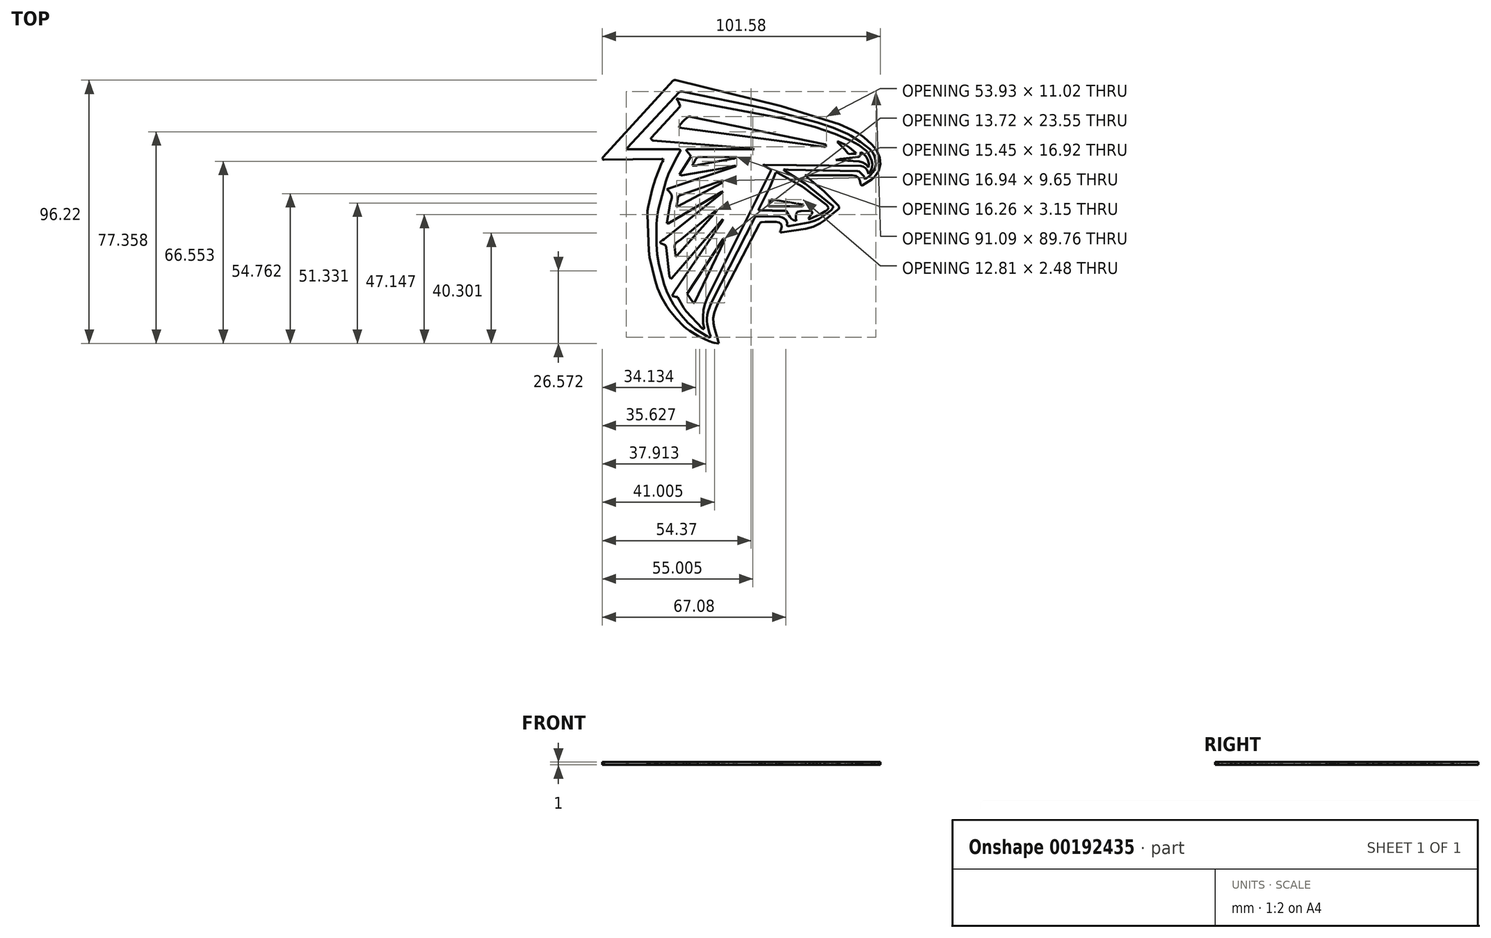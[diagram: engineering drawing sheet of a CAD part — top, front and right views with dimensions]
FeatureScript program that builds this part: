
annotation { "Feature Type Name" : "Feature", "Feature Type Description" : "" }
export const myFeature = defineFeature(function(context is Context, id is Id, definition is map)
    precondition{}
    {
        {
            var Q0;
            Q0=qCreatedBy(makeId("Top.planeOp"),FACE);
            var sketch = newSketch(context, id + "F0", { "sketchPlane" : qUnion([Q0])});
            skLineSegment(sketch, "E0", {"start": v(23.28, 13.3) * mm, "end": v(30.3, 7.5) * mm});
            skLineSegment(sketch, "E1", {"start": v(30.3, 7.5) * mm, "end": v(35.43, 2.3) * mm});
            skLineSegment(sketch, "E2", {"start": v(35.43, 2.3) * mm, "end": v(35.74, 1.85) * mm});
            skLineSegment(sketch, "E3", {"start": v(35.74, 1.85) * mm, "end": v(35.77, 1.44) * mm});
            skLineSegment(sketch, "E4", {"start": v(35.77, 1.44) * mm, "end": v(35.59, 1.07) * mm});
            skLineSegment(sketch, "E5", {"start": v(35.59, 1.07) * mm, "end": v(35.26, 0.74) * mm});
            skLineSegment(sketch, "E6", {"start": v(35.26, 0.74) * mm, "end": v(30.53, -3.08) * mm});
            skLineSegment(sketch, "E7", {"start": v(30.53, -3.08) * mm, "end": v(28.87, -4.22) * mm});
            skLineSegment(sketch, "E8", {"start": v(28.87, -4.22) * mm, "end": v(27.63, -4.88) * mm});
            skLineSegment(sketch, "E9", {"start": v(27.63, -4.88) * mm, "end": v(26.3, -5.42) * mm});
            skLineSegment(sketch, "E10", {"start": v(26.3, -5.42) * mm, "end": v(24.92, -5.85) * mm});
            skLineSegment(sketch, "E11", {"start": v(24.92, -5.85) * mm, "end": v(23.52, -6.18) * mm});
            skLineSegment(sketch, "E12", {"start": v(23.52, -6.18) * mm, "end": v(14.87, -7.46) * mm});
            skLineSegment(sketch, "E13", {"start": v(14.87, -7.46) * mm, "end": v(14.3, -7.46) * mm});
            skLineSegment(sketch, "E14", {"start": v(14.3, -7.46) * mm, "end": v(14.16, -7.29) * mm});
            skLineSegment(sketch, "E15", {"start": v(14.16, -7.29) * mm, "end": v(14.26, -6.99) * mm});
            skLineSegment(sketch, "E16", {"start": v(14.26, -6.99) * mm, "end": v(14.47, -6.6) * mm});
            skLineSegment(sketch, "E17", {"start": v(14.47, -6.6) * mm, "end": v(14.8, -5.5) * mm});
            skLineSegment(sketch, "E18", {"start": v(14.8, -5.5) * mm, "end": v(14.6, -4.6) * mm});
            skLineSegment(sketch, "E19", {"start": v(14.6, -4.6) * mm, "end": v(13.92, -3.95) * mm});
            skLineSegment(sketch, "E20", {"start": v(13.92, -3.95) * mm, "end": v(12.8, -3.69) * mm});
            skLineSegment(sketch, "E21", {"start": v(12.8, -3.69) * mm, "end": v(8.7, -3.66) * mm});
            skLineSegment(sketch, "E22", {"start": v(8.7, -3.66) * mm, "end": v(7.35, -3.78) * mm});
            skLineSegment(sketch, "E23", {"start": v(7.35, -3.78) * mm, "end": v(6.97, -3.98) * mm});
            skLineSegment(sketch, "E24", {"start": v(6.97, -3.98) * mm, "end": v(6.6, -4.42) * mm});
            skLineSegment(sketch, "E25", {"start": v(6.6, -4.42) * mm, "end": v(-8.52, -33.44) * mm});
            skLineSegment(sketch, "E26", {"start": v(-8.52, -33.44) * mm, "end": v(-9.27, -35.2) * mm});
            skLineSegment(sketch, "E27", {"start": v(-9.27, -35.2) * mm, "end": v(-9.87, -37) * mm});
            skLineSegment(sketch, "E28", {"start": v(-9.87, -37) * mm, "end": v(-10.2, -38.85) * mm});
            skLineSegment(sketch, "E29", {"start": v(-10.2, -38.85) * mm, "end": v(-10.15, -40.75) * mm});
            skLineSegment(sketch, "E30", {"start": v(-10.15, -40.75) * mm, "end": v(-9.86, -42.23) * mm});
            skLineSegment(sketch, "E31", {"start": v(-9.86, -42.23) * mm, "end": v(-8.51, -46.97) * mm});
            skLineSegment(sketch, "E32", {"start": v(-8.51, -46.97) * mm, "end": v(-8.26, -48.11) * mm});
            skLineSegment(sketch, "E33", {"start": v(-8.26, -48.11) * mm, "end": v(-9.85, -47.87) * mm});
            skLineSegment(sketch, "E34", {"start": v(-9.85, -47.87) * mm, "end": v(-10.37, -47.73) * mm});
            skLineSegment(sketch, "E35", {"start": v(-10.37, -47.73) * mm, "end": v(-11.81, -47.2) * mm});
            skLineSegment(sketch, "E36", {"start": v(-11.81, -47.2) * mm, "end": v(-15.84, -45.4) * mm});
            skLineSegment(sketch, "E37", {"start": v(-15.84, -45.4) * mm, "end": v(-18.95, -43.47) * mm});
            skLineSegment(sketch, "E38", {"start": v(-18.95, -43.47) * mm, "end": v(-20.04, -42.66) * mm});
            skLineSegment(sketch, "E39", {"start": v(-20.04, -42.66) * mm, "end": v(-21.05, -41.78) * mm});
            skLineSegment(sketch, "E40", {"start": v(-21.05, -41.78) * mm, "end": v(-23.76, -38.96) * mm});
            skLineSegment(sketch, "E41", {"start": v(-23.76, -38.96) * mm, "end": v(-26.2, -35.92) * mm});
            skLineSegment(sketch, "E42", {"start": v(-26.2, -35.92) * mm, "end": v(-27.26, -34.37) * mm});
            skLineSegment(sketch, "E43", {"start": v(-27.26, -34.37) * mm, "end": v(-29.11, -31.1) * mm});
            skLineSegment(sketch, "E44", {"start": v(-29.11, -31.1) * mm, "end": v(-30.55, -28) * mm});
            skLineSegment(sketch, "E45", {"start": v(-30.55, -28) * mm, "end": v(-31.52, -25.04) * mm});
            skLineSegment(sketch, "E46", {"start": v(-31.52, -25.04) * mm, "end": v(-33.47, -16.6) * mm});
            skLineSegment(sketch, "E47", {"start": v(-33.47, -16.6) * mm, "end": v(-33.8, -14.27) * mm});
            skLineSegment(sketch, "E48", {"start": v(-33.8, -14.27) * mm, "end": v(-34.31, -1.16) * mm});
            skLineSegment(sketch, "E49", {"start": v(-34.31, -1.16) * mm, "end": v(-34.24, 0.31) * mm});
            skLineSegment(sketch, "E50", {"start": v(-34.24, 0.31) * mm, "end": v(-34.04, 1.8) * mm});
            skLineSegment(sketch, "E51", {"start": v(-34.04, 1.8) * mm, "end": v(-32.46, 8.38) * mm});
            skLineSegment(sketch, "E52", {"start": v(-32.46, 8.38) * mm, "end": v(-31.33, 12) * mm});
            skLineSegment(sketch, "E53", {"start": v(-31.33, 12) * mm, "end": v(-29.05, 17.9) * mm});
            skLineSegment(sketch, "E54", {"start": v(-29.05, 17.9) * mm, "end": v(-29, 18) * mm});
            skLineSegment(sketch, "E55", {"start": v(-29, 18) * mm, "end": v(-28.93, 18.1) * mm});
            skLineSegment(sketch, "E56", {"start": v(-28.93, 18.1) * mm, "end": v(-28.78, 18.29) * mm});
            skLineSegment(sketch, "E57", {"start": v(-28.78, 18.29) * mm, "end": v(-28.44, 18.96) * mm});
            skLineSegment(sketch, "E58", {"start": v(-28.44, 18.96) * mm, "end": v(-28.57, 19.27) * mm});
            skLineSegment(sketch, "E59", {"start": v(-28.57, 19.27) * mm, "end": v(-29, 19.36) * mm});
            skLineSegment(sketch, "E60", {"start": v(-29, 19.36) * mm, "end": v(-50.12, 19.08) * mm});
            skLineSegment(sketch, "E61", {"start": v(-50.12, 19.08) * mm, "end": v(-50.29, 19.1) * mm});
            skLineSegment(sketch, "E62", {"start": v(-50.29, 19.1) * mm, "end": v(-50.45, 19.14) * mm});
            skLineSegment(sketch, "E63", {"start": v(-50.45, 19.14) * mm, "end": v(-50.8, 19.24) * mm});
            skLineSegment(sketch, "E64", {"start": v(-50.8, 19.24) * mm, "end": v(-50.67, 19.59) * mm});
            skLineSegment(sketch, "E65", {"start": v(-50.67, 19.59) * mm, "end": v(-50.6, 19.75) * mm});
            skLineSegment(sketch, "E66", {"start": v(-50.6, 19.75) * mm, "end": v(-50.5, 19.9) * mm});
            skLineSegment(sketch, "E67", {"start": v(-50.5, 19.9) * mm, "end": v(-24.84, 47.95) * mm});
            skLineSegment(sketch, "E68", {"start": v(-24.84, 47.95) * mm, "end": v(-24.67, 48.06) * mm});
            skLineSegment(sketch, "E69", {"start": v(-24.67, 48.06) * mm, "end": v(-24.44, 48.1) * mm});
            skLineSegment(sketch, "E70", {"start": v(-24.44, 48.1) * mm, "end": v(-24.19, 48.11) * mm});
            skLineSegment(sketch, "E71", {"start": v(-24.19, 48.11) * mm, "end": v(-23.95, 48.1) * mm});
            skLineSegment(sketch, "E72", {"start": v(-23.95, 48.1) * mm, "end": v(14.66, 38.66) * mm});
            skLineSegment(sketch, "E73", {"start": v(14.66, 38.66) * mm, "end": v(35.83, 31.94) * mm});
            skLineSegment(sketch, "E74", {"start": v(35.83, 31.94) * mm, "end": v(40.3, 30) * mm});
            skLineSegment(sketch, "E75", {"start": v(40.3, 30) * mm, "end": v(42.7, 28.71) * mm});
            skLineSegment(sketch, "E76", {"start": v(42.7, 28.71) * mm, "end": v(43.83, 28) * mm});
            skLineSegment(sketch, "E77", {"start": v(43.83, 28) * mm, "end": v(44.9, 27.19) * mm});
            skLineSegment(sketch, "E78", {"start": v(44.9, 27.19) * mm, "end": v(47.52, 24.76) * mm});
            skLineSegment(sketch, "E79", {"start": v(47.52, 24.76) * mm, "end": v(48.7, 23.44) * mm});
            skLineSegment(sketch, "E80", {"start": v(48.7, 23.44) * mm, "end": v(49.68, 22) * mm});
            skLineSegment(sketch, "E81", {"start": v(49.68, 22) * mm, "end": v(50.55, 19.82) * mm});
            skLineSegment(sketch, "E82", {"start": v(50.55, 19.82) * mm, "end": v(50.8, 17.38) * mm});
            skLineSegment(sketch, "E83", {"start": v(50.8, 17.38) * mm, "end": v(50.2, 14.9) * mm});
            skLineSegment(sketch, "E84", {"start": v(50.2, 14.9) * mm, "end": v(48.62, 12.64) * mm});
            skLineSegment(sketch, "E85", {"start": v(48.62, 12.64) * mm, "end": v(47.61, 11.79) * mm});
            skLineSegment(sketch, "E86", {"start": v(47.61, 11.79) * mm, "end": v(44.24, 9.62) * mm});
            skLineSegment(sketch, "E87", {"start": v(44.24, 9.62) * mm, "end": v(44.09, 9.65) * mm});
            skLineSegment(sketch, "E88", {"start": v(44.09, 9.65) * mm, "end": v(43.86, 9.8) * mm});
            skLineSegment(sketch, "E89", {"start": v(43.86, 9.8) * mm, "end": v(43.64, 9.98) * mm});
            skLineSegment(sketch, "E90", {"start": v(43.64, 9.98) * mm, "end": v(43.55, 10.14) * mm});
            skLineSegment(sketch, "E91", {"start": v(43.55, 10.14) * mm, "end": v(43.37, 11.44) * mm});
            skLineSegment(sketch, "E92", {"start": v(43.37, 11.44) * mm, "end": v(42.82, 12.43) * mm});
            skLineSegment(sketch, "E93", {"start": v(42.82, 12.43) * mm, "end": v(41.89, 13.06) * mm});
            skLineSegment(sketch, "E94", {"start": v(41.89, 13.06) * mm, "end": v(40.58, 13.3) * mm});
            skLineSegment(sketch, "E95", {"start": v(40.58, 13.3) * mm, "end": v(23.45, 13.34) * mm});
            skLineSegment(sketch, "E96", {"start": v(23.45, 13.34) * mm, "end": v(23.37, 13.33) * mm});
            skLineSegment(sketch, "E97", {"start": v(23.37, 13.33) * mm, "end": v(23.31, 13.32) * mm});
            skLineSegment(sketch, "E98", {"start": v(23.31, 13.32) * mm, "end": v(23.28, 13.3) * mm});
            skLineSegment(sketch, "E99", {"start": v(23.28, 13.3) * mm, "end": v(23.28, 13.3) * mm});
            skLineSegment(sketch, "E100", {"start": v(-32.1, 22.82) * mm, "end": v(-22.6, 22.8) * mm});
            skLineSegment(sketch, "E101", {"start": v(-22.6, 22.8) * mm, "end": v(-22.47, 22.73) * mm});
            skLineSegment(sketch, "E102", {"start": v(-22.47, 22.73) * mm, "end": v(-22.32, 22.58) * mm});
            skLineSegment(sketch, "E103", {"start": v(-22.32, 22.58) * mm, "end": v(-22.2, 22.42) * mm});
            skLineSegment(sketch, "E104", {"start": v(-22.2, 22.42) * mm, "end": v(-22.18, 22.32) * mm});
            skLineSegment(sketch, "E105", {"start": v(-22.18, 22.32) * mm, "end": v(-23.47, 20.09) * mm});
            skLineSegment(sketch, "E106", {"start": v(-23.47, 20.09) * mm, "end": v(-26.46, 14.04) * mm});
            skLineSegment(sketch, "E107", {"start": v(-26.46, 14.04) * mm, "end": v(-27.54, 11.12) * mm});
            skLineSegment(sketch, "E108", {"start": v(-27.54, 11.12) * mm, "end": v(-30.26, 0.8) * mm});
            skLineSegment(sketch, "E109", {"start": v(-30.26, 0.8) * mm, "end": v(-30.7, -1.77) * mm});
            skLineSegment(sketch, "E110", {"start": v(-30.7, -1.77) * mm, "end": v(-30.9, -4.37) * mm});
            skLineSegment(sketch, "E111", {"start": v(-30.9, -4.37) * mm, "end": v(-30.97, -11.85) * mm});
            skLineSegment(sketch, "E112", {"start": v(-30.97, -11.85) * mm, "end": v(-30.7, -15.58) * mm});
            skLineSegment(sketch, "E113", {"start": v(-30.7, -15.58) * mm, "end": v(-30.04, -19.28) * mm});
            skLineSegment(sketch, "E114", {"start": v(-30.04, -19.28) * mm, "end": v(-28.11, -26.54) * mm});
            skLineSegment(sketch, "E115", {"start": v(-28.11, -26.54) * mm, "end": v(-27.23, -29) * mm});
            skLineSegment(sketch, "E116", {"start": v(-27.23, -29) * mm, "end": v(-26.14, -31.4) * mm});
            skLineSegment(sketch, "E117", {"start": v(-26.14, -31.4) * mm, "end": v(-24.7, -33.94) * mm});
            skLineSegment(sketch, "E118", {"start": v(-24.7, -33.94) * mm, "end": v(-23.9, -35.17) * mm});
            skLineSegment(sketch, "E119", {"start": v(-23.9, -35.17) * mm, "end": v(-21.91, -37.77) * mm});
            skLineSegment(sketch, "E120", {"start": v(-21.91, -37.77) * mm, "end": v(-19.5, -40.48) * mm});
            skLineSegment(sketch, "E121", {"start": v(-19.5, -40.48) * mm, "end": v(-18.18, -41.72) * mm});
            skLineSegment(sketch, "E122", {"start": v(-18.18, -41.72) * mm, "end": v(-16.84, -42.77) * mm});
            skLineSegment(sketch, "E123", {"start": v(-16.84, -42.77) * mm, "end": v(-12.3, -45.64) * mm});
            skLineSegment(sketch, "E124", {"start": v(-12.3, -45.64) * mm, "end": v(-12.1, -45.73) * mm});
            skLineSegment(sketch, "E125", {"start": v(-12.1, -45.73) * mm, "end": v(-11.88, -45.8) * mm});
            skLineSegment(sketch, "E126", {"start": v(-11.88, -45.8) * mm, "end": v(-11.67, -45.85) * mm});
            skLineSegment(sketch, "E127", {"start": v(-11.67, -45.85) * mm, "end": v(-11.52, -45.83) * mm});
            skLineSegment(sketch, "E128", {"start": v(-11.52, -45.83) * mm, "end": v(-11.35, -45.77) * mm});
            skLineSegment(sketch, "E129", {"start": v(-11.35, -45.77) * mm, "end": v(-11.22, -45.7) * mm});
            skLineSegment(sketch, "E130", {"start": v(-11.22, -45.7) * mm, "end": v(-11.17, -45.65) * mm});
            skLineSegment(sketch, "E131", {"start": v(-11.17, -45.65) * mm, "end": v(-11.72, -43.85) * mm});
            skLineSegment(sketch, "E132", {"start": v(-11.72, -43.85) * mm, "end": v(-12.35, -41.06) * mm});
            skLineSegment(sketch, "E133", {"start": v(-12.35, -41.06) * mm, "end": v(-12.51, -39.97) * mm});
            skLineSegment(sketch, "E134", {"start": v(-12.51, -39.97) * mm, "end": v(-12.54, -38.89) * mm});
            skLineSegment(sketch, "E135", {"start": v(-12.54, -38.89) * mm, "end": v(-12.4, -37.75) * mm});
            skLineSegment(sketch, "E136", {"start": v(-12.4, -37.75) * mm, "end": v(-12.14, -36.61) * mm});
            skLineSegment(sketch, "E137", {"start": v(-12.14, -36.61) * mm, "end": v(-11.4, -34.39) * mm});
            skLineSegment(sketch, "E138", {"start": v(-11.4, -34.39) * mm, "end": v(-10.41, -32.1) * mm});
            skLineSegment(sketch, "E139", {"start": v(-10.41, -32.1) * mm, "end": v(4.69, -2.53) * mm});
            skLineSegment(sketch, "E140", {"start": v(4.69, -2.53) * mm, "end": v(5.03, -2.04) * mm});
            skLineSegment(sketch, "E141", {"start": v(5.03, -2.04) * mm, "end": v(5.38, -1.82) * mm});
            skLineSegment(sketch, "E142", {"start": v(5.38, -1.82) * mm, "end": v(9.67, -1.69) * mm});
            skLineSegment(sketch, "E143", {"start": v(9.67, -1.69) * mm, "end": v(13.96, -1.82) * mm});
            skLineSegment(sketch, "E144", {"start": v(13.96, -1.82) * mm, "end": v(14.88, -1.99) * mm});
            skLineSegment(sketch, "E145", {"start": v(14.88, -1.99) * mm, "end": v(15.71, -2.4) * mm});
            skLineSegment(sketch, "E146", {"start": v(15.71, -2.4) * mm, "end": v(16.37, -3.08) * mm});
            skLineSegment(sketch, "E147", {"start": v(16.37, -3.08) * mm, "end": v(16.76, -4.1) * mm});
            skLineSegment(sketch, "E148", {"start": v(16.76, -4.1) * mm, "end": v(16.72, -4.9) * mm});
            skLineSegment(sketch, "E149", {"start": v(16.72, -4.9) * mm, "end": v(16.91, -5.22) * mm});
            skLineSegment(sketch, "E150", {"start": v(16.91, -5.22) * mm, "end": v(17.53, -5.25) * mm});
            skLineSegment(sketch, "E151", {"start": v(17.53, -5.25) * mm, "end": v(24.58, -3.94) * mm});
            skLineSegment(sketch, "E152", {"start": v(24.58, -3.94) * mm, "end": v(26.85, -3.27) * mm});
            skLineSegment(sketch, "E153", {"start": v(26.85, -3.27) * mm, "end": v(28.45, -2.53) * mm});
            skLineSegment(sketch, "E154", {"start": v(28.45, -2.53) * mm, "end": v(29.96, -1.55) * mm});
            skLineSegment(sketch, "E155", {"start": v(29.96, -1.55) * mm, "end": v(32.9, 0.64) * mm});
            skLineSegment(sketch, "E156", {"start": v(32.9, 0.64) * mm, "end": v(33.17, 0.95) * mm});
            skLineSegment(sketch, "E157", {"start": v(33.17, 0.95) * mm, "end": v(33.41, 1.38) * mm});
            skLineSegment(sketch, "E158", {"start": v(33.41, 1.38) * mm, "end": v(33.56, 1.77) * mm});
            skLineSegment(sketch, "E159", {"start": v(33.56, 1.77) * mm, "end": v(33.57, 1.98) * mm});
            skLineSegment(sketch, "E160", {"start": v(33.57, 1.98) * mm, "end": v(23.37, 10.22) * mm});
            skLineSegment(sketch, "E161", {"start": v(23.37, 10.22) * mm, "end": v(15.86, 14.94) * mm});
            skLineSegment(sketch, "E162", {"start": v(15.86, 14.94) * mm, "end": v(15.75, 15.03) * mm});
            skLineSegment(sketch, "E163", {"start": v(15.75, 15.03) * mm, "end": v(15.66, 15.14) * mm});
            skLineSegment(sketch, "E164", {"start": v(15.66, 15.14) * mm, "end": v(15.48, 15.38) * mm});
            skLineSegment(sketch, "E165", {"start": v(15.48, 15.38) * mm, "end": v(15.72, 15.46) * mm});
            skLineSegment(sketch, "E166", {"start": v(15.72, 15.46) * mm, "end": v(15.83, 15.49) * mm});
            skLineSegment(sketch, "E167", {"start": v(15.83, 15.49) * mm, "end": v(15.94, 15.5) * mm});
            skLineSegment(sketch, "E168", {"start": v(15.94, 15.5) * mm, "end": v(17.22, 15.3) * mm});
            skLineSegment(sketch, "E169", {"start": v(17.22, 15.3) * mm, "end": v(42.44, 14.87) * mm});
            skLineSegment(sketch, "E170", {"start": v(42.44, 14.87) * mm, "end": v(43.05, 14.67) * mm});
            skLineSegment(sketch, "E171", {"start": v(43.05, 14.67) * mm, "end": v(43.63, 14.22) * mm});
            skLineSegment(sketch, "E172", {"start": v(43.63, 14.22) * mm, "end": v(44.78, 13.13) * mm});
            skLineSegment(sketch, "E173", {"start": v(44.78, 13.13) * mm, "end": v(44.93, 12.73) * mm});
            skLineSegment(sketch, "E174", {"start": v(44.93, 12.73) * mm, "end": v(45.02, 12.22) * mm});
            skLineSegment(sketch, "E175", {"start": v(45.02, 12.22) * mm, "end": v(45.29, 11.98) * mm});
            skLineSegment(sketch, "E176", {"start": v(45.29, 11.98) * mm, "end": v(46, 12.38) * mm});
            skLineSegment(sketch, "E177", {"start": v(46, 12.38) * mm, "end": v(47.13, 13.38) * mm});
            skLineSegment(sketch, "E178", {"start": v(47.13, 13.38) * mm, "end": v(48.09, 14.47) * mm});
            skLineSegment(sketch, "E179", {"start": v(48.09, 14.47) * mm, "end": v(48.79, 15.71) * mm});
            skLineSegment(sketch, "E180", {"start": v(48.79, 15.71) * mm, "end": v(49.13, 17.16) * mm});
            skLineSegment(sketch, "E181", {"start": v(49.13, 17.16) * mm, "end": v(49.1, 18.8) * mm});
            skLineSegment(sketch, "E182", {"start": v(49.1, 18.8) * mm, "end": v(48.74, 20.35) * mm});
            skLineSegment(sketch, "E183", {"start": v(48.74, 20.35) * mm, "end": v(48.03, 21.74) * mm});
            skLineSegment(sketch, "E184", {"start": v(48.03, 21.74) * mm, "end": v(46.94, 22.93) * mm});
            skLineSegment(sketch, "E185", {"start": v(46.94, 22.93) * mm, "end": v(43.61, 25.5) * mm});
            skLineSegment(sketch, "E186", {"start": v(43.61, 25.5) * mm, "end": v(40.1, 27.82) * mm});
            skLineSegment(sketch, "E187", {"start": v(40.1, 27.82) * mm, "end": v(38.89, 28.49) * mm});
            skLineSegment(sketch, "E188", {"start": v(38.89, 28.49) * mm, "end": v(33.57, 30.67) * mm});
            skLineSegment(sketch, "E189", {"start": v(33.57, 30.67) * mm, "end": v(27.9, 32.6) * mm});
            skLineSegment(sketch, "E190", {"start": v(27.9, 32.6) * mm, "end": v(8.3, 37.88) * mm});
            skLineSegment(sketch, "E191", {"start": v(8.3, 37.88) * mm, "end": v(-21.55, 43.9) * mm});
            skLineSegment(sketch, "E192", {"start": v(-21.55, 43.9) * mm, "end": v(-22, 43.92) * mm});
            skLineSegment(sketch, "E193", {"start": v(-22, 43.92) * mm, "end": v(-22.42, 43.86) * mm});
            skLineSegment(sketch, "E194", {"start": v(-22.42, 43.86) * mm, "end": v(-22.72, 43.7) * mm});
            skLineSegment(sketch, "E195", {"start": v(-22.72, 43.7) * mm, "end": v(-41.65, 23.37) * mm});
            skLineSegment(sketch, "E196", {"start": v(-41.65, 23.37) * mm, "end": v(-41.74, 23.26) * mm});
            skLineSegment(sketch, "E197", {"start": v(-41.74, 23.26) * mm, "end": v(-41.97, 22.92) * mm});
            skLineSegment(sketch, "E198", {"start": v(-41.97, 22.92) * mm, "end": v(-41.5, 22.83) * mm});
            skLineSegment(sketch, "E199", {"start": v(-41.5, 22.83) * mm, "end": v(-41.35, 22.82) * mm});
            skLineSegment(sketch, "E200", {"start": v(-41.35, 22.82) * mm, "end": v(-32.1, 22.82) * mm});
            skLineSegment(sketch, "E201", {"start": v(-2, 16.83) * mm, "end": v(-4.63, 16.43) * mm});
            skLineSegment(sketch, "E202", {"start": v(-4.63, 16.43) * mm, "end": v(-6.82, 15.92) * mm});
            skLineSegment(sketch, "E203", {"start": v(-6.82, 15.92) * mm, "end": v(-21.55, 13.34) * mm});
            skLineSegment(sketch, "E204", {"start": v(-21.55, 13.34) * mm, "end": v(-21.8, 13.35) * mm});
            skLineSegment(sketch, "E205", {"start": v(-21.8, 13.35) * mm, "end": v(-22.08, 13.41) * mm});
            skLineSegment(sketch, "E206", {"start": v(-22.08, 13.41) * mm, "end": v(-22.62, 13.6) * mm});
            skLineSegment(sketch, "E207", {"start": v(-22.62, 13.6) * mm, "end": v(-18.44, 20.18) * mm});
            skLineSegment(sketch, "E208", {"start": v(-18.44, 20.18) * mm, "end": v(-18.46, 20.38) * mm});
            skLineSegment(sketch, "E209", {"start": v(-18.46, 20.38) * mm, "end": v(-18.61, 20.66) * mm});
            skLineSegment(sketch, "E210", {"start": v(-18.61, 20.66) * mm, "end": v(-19.26, 21.51) * mm});
            skLineSegment(sketch, "E211", {"start": v(-19.26, 21.51) * mm, "end": v(-19.92, 22.25) * mm});
            skLineSegment(sketch, "E212", {"start": v(-19.92, 22.25) * mm, "end": v(-19.98, 22.36) * mm});
            skLineSegment(sketch, "E213", {"start": v(-19.98, 22.36) * mm, "end": v(-20.02, 22.5) * mm});
            skLineSegment(sketch, "E214", {"start": v(-20.02, 22.5) * mm, "end": v(-20.03, 22.61) * mm});
            skLineSegment(sketch, "E215", {"start": v(-20.03, 22.61) * mm, "end": v(-20.02, 22.67) * mm});
            skLineSegment(sketch, "E216", {"start": v(-20.02, 22.67) * mm, "end": v(-19.9, 22.73) * mm});
            skLineSegment(sketch, "E217", {"start": v(-19.9, 22.73) * mm, "end": v(-19.77, 22.78) * mm});
            skLineSegment(sketch, "E218", {"start": v(-19.77, 22.78) * mm, "end": v(-19.64, 22.8) * mm});
            skLineSegment(sketch, "E219", {"start": v(-19.64, 22.8) * mm, "end": v(-19.5, 22.81) * mm});
            skLineSegment(sketch, "E220", {"start": v(-19.5, 22.81) * mm, "end": v(3.8, 22.86) * mm});
            skLineSegment(sketch, "E221", {"start": v(3.8, 22.86) * mm, "end": v(4.69, 22.91) * mm});
            skLineSegment(sketch, "E222", {"start": v(4.69, 22.91) * mm, "end": v(4.15, 23.08) * mm});
            skLineSegment(sketch, "E223", {"start": v(4.15, 23.08) * mm, "end": v(4.08, 23.09) * mm});
            skLineSegment(sketch, "E224", {"start": v(4.08, 23.09) * mm, "end": v(-32.26, 26.04) * mm});
            skLineSegment(sketch, "E225", {"start": v(-32.26, 26.04) * mm, "end": v(-32.5, 26.14) * mm});
            skLineSegment(sketch, "E226", {"start": v(-32.5, 26.14) * mm, "end": v(-32.76, 26.36) * mm});
            skLineSegment(sketch, "E227", {"start": v(-32.76, 26.36) * mm, "end": v(-32.94, 26.6) * mm});
            skLineSegment(sketch, "E228", {"start": v(-32.94, 26.6) * mm, "end": v(-33, 26.78) * mm});
            skLineSegment(sketch, "E229", {"start": v(-33, 26.78) * mm, "end": v(-32.85, 27.06) * mm});
            skLineSegment(sketch, "E230", {"start": v(-32.85, 27.06) * mm, "end": v(-22.39, 38.38) * mm});
            skLineSegment(sketch, "E231", {"start": v(-22.39, 38.38) * mm, "end": v(-22.35, 38.64) * mm});
            skLineSegment(sketch, "E232", {"start": v(-22.35, 38.64) * mm, "end": v(-22.46, 39.02) * mm});
            skLineSegment(sketch, "E233", {"start": v(-22.46, 39.02) * mm, "end": v(-23, 40.2) * mm});
            skLineSegment(sketch, "E234", {"start": v(-23, 40.2) * mm, "end": v(-23.69, 41.35) * mm});
            skLineSegment(sketch, "E235", {"start": v(-23.69, 41.35) * mm, "end": v(14.91, 34.12) * mm});
            skLineSegment(sketch, "E236", {"start": v(14.91, 34.12) * mm, "end": v(26.99, 30.97) * mm});
            skLineSegment(sketch, "E237", {"start": v(26.99, 30.97) * mm, "end": v(34.3, 28.46) * mm});
            skLineSegment(sketch, "E238", {"start": v(34.3, 28.46) * mm, "end": v(40.23, 25.93) * mm});
            skLineSegment(sketch, "E239", {"start": v(40.23, 25.93) * mm, "end": v(43.01, 24.34) * mm});
            skLineSegment(sketch, "E240", {"start": v(43.01, 24.34) * mm, "end": v(45.58, 22.38) * mm});
            skLineSegment(sketch, "E241", {"start": v(45.58, 22.38) * mm, "end": v(46.24, 21.61) * mm});
            skLineSegment(sketch, "E242", {"start": v(46.24, 21.61) * mm, "end": v(46.76, 20.69) * mm});
            skLineSegment(sketch, "E243", {"start": v(46.76, 20.69) * mm, "end": v(47.62, 18.68) * mm});
            skLineSegment(sketch, "E244", {"start": v(47.62, 18.68) * mm, "end": v(47.94, 17.45) * mm});
            skLineSegment(sketch, "E245", {"start": v(47.94, 17.45) * mm, "end": v(47.85, 16.28) * mm});
            skLineSegment(sketch, "E246", {"start": v(47.85, 16.28) * mm, "end": v(47.41, 15.17) * mm});
            skLineSegment(sketch, "E247", {"start": v(47.41, 15.17) * mm, "end": v(46.72, 14.12) * mm});
            skLineSegment(sketch, "E248", {"start": v(46.72, 14.12) * mm, "end": v(46.66, 14.05) * mm});
            skLineSegment(sketch, "E249", {"start": v(46.66, 14.05) * mm, "end": v(46.47, 13.87) * mm});
            skLineSegment(sketch, "E250", {"start": v(46.47, 13.87) * mm, "end": v(46.36, 14.16) * mm});
            skLineSegment(sketch, "E251", {"start": v(46.36, 14.16) * mm, "end": v(46.33, 14.25) * mm});
            skLineSegment(sketch, "E252", {"start": v(46.33, 14.25) * mm, "end": v(45.98, 15.23) * mm});
            skLineSegment(sketch, "E253", {"start": v(45.98, 15.23) * mm, "end": v(45.42, 16.02) * mm});
            skLineSegment(sketch, "E254", {"start": v(45.42, 16.02) * mm, "end": v(44.66, 16.56) * mm});
            skLineSegment(sketch, "E255", {"start": v(44.66, 16.56) * mm, "end": v(43.72, 16.79) * mm});
            skLineSegment(sketch, "E256", {"start": v(43.72, 16.79) * mm, "end": v(8.5, 17.14) * mm});
            skLineSegment(sketch, "E257", {"start": v(8.5, 17.14) * mm, "end": v(8.34, 17.13) * mm});
            skLineSegment(sketch, "E258", {"start": v(8.34, 17.13) * mm, "end": v(7.87, 17.05) * mm});
            skLineSegment(sketch, "E259", {"start": v(7.87, 17.05) * mm, "end": v(10.82, 15.52) * mm});
            skLineSegment(sketch, "E260", {"start": v(10.82, 15.52) * mm, "end": v(10.86, 15.37) * mm});
            skLineSegment(sketch, "E261", {"start": v(10.86, 15.37) * mm, "end": v(10.83, 15.08) * mm});
            skLineSegment(sketch, "E262", {"start": v(10.83, 15.08) * mm, "end": v(10.75, 14.74) * mm});
            skLineSegment(sketch, "E263", {"start": v(10.75, 14.74) * mm, "end": v(10.64, 14.45) * mm});
            skLineSegment(sketch, "E264", {"start": v(10.64, 14.45) * mm, "end": v(-12.4, -31.56) * mm});
            skLineSegment(sketch, "E265", {"start": v(-12.4, -31.56) * mm, "end": v(-13.3, -33.76) * mm});
            skLineSegment(sketch, "E266", {"start": v(-13.3, -33.76) * mm, "end": v(-13.82, -36) * mm});
            skLineSegment(sketch, "E267", {"start": v(-13.82, -36) * mm, "end": v(-13.99, -38.3) * mm});
            skLineSegment(sketch, "E268", {"start": v(-13.99, -38.3) * mm, "end": v(-13.88, -40.66) * mm});
            skLineSegment(sketch, "E269", {"start": v(-13.88, -40.66) * mm, "end": v(-13.6, -42.4) * mm});
            skLineSegment(sketch, "E270", {"start": v(-13.6, -42.4) * mm, "end": v(-13.6, -42.5) * mm});
            skLineSegment(sketch, "E271", {"start": v(-13.6, -42.5) * mm, "end": v(-13.6, -42.62) * mm});
            skLineSegment(sketch, "E272", {"start": v(-13.6, -42.62) * mm, "end": v(-13.64, -42.71) * mm});
            skLineSegment(sketch, "E273", {"start": v(-13.64, -42.71) * mm, "end": v(-13.68, -42.76) * mm});
            skLineSegment(sketch, "E274", {"start": v(-13.68, -42.76) * mm, "end": v(-13.8, -42.79) * mm});
            skLineSegment(sketch, "E275", {"start": v(-13.8, -42.79) * mm, "end": v(-13.92, -42.79) * mm});
            skLineSegment(sketch, "E276", {"start": v(-13.92, -42.79) * mm, "end": v(-14.04, -42.77) * mm});
            skLineSegment(sketch, "E277", {"start": v(-14.04, -42.77) * mm, "end": v(-14.13, -42.72) * mm});
            skLineSegment(sketch, "E278", {"start": v(-14.13, -42.72) * mm, "end": v(-20.2, -36.3) * mm});
            skLineSegment(sketch, "E279", {"start": v(-20.2, -36.3) * mm, "end": v(-21.03, -35.12) * mm});
            skLineSegment(sketch, "E280", {"start": v(-21.03, -35.12) * mm, "end": v(-23.15, -31.26) * mm});
            skLineSegment(sketch, "E281", {"start": v(-23.15, -31.26) * mm, "end": v(-23.26, -31.18) * mm});
            skLineSegment(sketch, "E282", {"start": v(-23.26, -31.18) * mm, "end": v(-23.44, -31.14) * mm});
            skLineSegment(sketch, "E283", {"start": v(-23.44, -31.14) * mm, "end": v(-23.83, -31.08) * mm});
            skLineSegment(sketch, "E284", {"start": v(-23.83, -31.08) * mm, "end": v(-25.27, -30.7) * mm});
            skLineSegment(sketch, "E285", {"start": v(-25.27, -30.7) * mm, "end": v(-24.56, -29.51) * mm});
            skLineSegment(sketch, "E286", {"start": v(-24.56, -29.51) * mm, "end": v(-6.73, -3.24) * mm});
            skLineSegment(sketch, "E287", {"start": v(-6.73, -3.24) * mm, "end": v(-6.7, -3.15) * mm});
            skLineSegment(sketch, "E288", {"start": v(-6.7, -3.15) * mm, "end": v(-6.7, -3.03) * mm});
            skLineSegment(sketch, "E289", {"start": v(-6.7, -3.03) * mm, "end": v(-6.72, -2.8) * mm});
            skLineSegment(sketch, "E290", {"start": v(-6.72, -2.8) * mm, "end": v(-6.93, -2.98) * mm});
            skLineSegment(sketch, "E291", {"start": v(-6.93, -2.98) * mm, "end": v(-25.36, -24.28) * mm});
            skLineSegment(sketch, "E292", {"start": v(-25.36, -24.28) * mm, "end": v(-25.45, -24.35) * mm});
            skLineSegment(sketch, "E293", {"start": v(-25.45, -24.35) * mm, "end": v(-25.58, -24.42) * mm});
            skLineSegment(sketch, "E294", {"start": v(-25.58, -24.42) * mm, "end": v(-25.7, -24.46) * mm});
            skLineSegment(sketch, "E295", {"start": v(-25.7, -24.46) * mm, "end": v(-25.75, -24.47) * mm});
            skLineSegment(sketch, "E296", {"start": v(-25.75, -24.47) * mm, "end": v(-26.03, -24) * mm});
            skLineSegment(sketch, "E297", {"start": v(-26.03, -24) * mm, "end": v(-26.14, -23.76) * mm});
            skLineSegment(sketch, "E298", {"start": v(-26.14, -23.76) * mm, "end": v(-26.2, -23.52) * mm});
            skLineSegment(sketch, "E299", {"start": v(-26.2, -23.52) * mm, "end": v(-27.4, -13.07) * mm});
            skLineSegment(sketch, "E300", {"start": v(-27.4, -13.07) * mm, "end": v(-27.51, -12.55) * mm});
            skLineSegment(sketch, "E301", {"start": v(-27.51, -12.55) * mm, "end": v(-27.62, -12.37) * mm});
            skLineSegment(sketch, "E302", {"start": v(-27.62, -12.37) * mm, "end": v(-27.8, -12.2) * mm});
            skLineSegment(sketch, "E303", {"start": v(-27.8, -12.2) * mm, "end": v(-28.04, -12.08) * mm});
            skLineSegment(sketch, "E304", {"start": v(-28.04, -12.08) * mm, "end": v(-28.27, -12) * mm});
            skLineSegment(sketch, "E305", {"start": v(-28.27, -12) * mm, "end": v(-29.51, -11.45) * mm});
            skLineSegment(sketch, "E306", {"start": v(-29.51, -11.45) * mm, "end": v(-29.5, -10.93) * mm});
            skLineSegment(sketch, "E307", {"start": v(-29.5, -10.93) * mm, "end": v(-28.85, -10.45) * mm});
            skLineSegment(sketch, "E308", {"start": v(-28.85, -10.45) * mm, "end": v(-28.22, -10.05) * mm});
            skLineSegment(sketch, "E309", {"start": v(-28.22, -10.05) * mm, "end": v(-6.9, 7.04) * mm});
            skLineSegment(sketch, "E310", {"start": v(-6.9, 7.04) * mm, "end": v(-6.85, 7.1) * mm});
            skLineSegment(sketch, "E311", {"start": v(-6.85, 7.1) * mm, "end": v(-6.7, 7.32) * mm});
            skLineSegment(sketch, "E312", {"start": v(-6.7, 7.32) * mm, "end": v(-6.97, 7.33) * mm});
            skLineSegment(sketch, "E313", {"start": v(-6.97, 7.33) * mm, "end": v(-7.1, 7.33) * mm});
            skLineSegment(sketch, "E314", {"start": v(-7.1, 7.33) * mm, "end": v(-7.22, 7.3) * mm});
            skLineSegment(sketch, "E315", {"start": v(-7.22, 7.3) * mm, "end": v(-26.72, -4.34) * mm});
            skLineSegment(sketch, "E316", {"start": v(-26.72, -4.34) * mm, "end": v(-26.82, -4.32) * mm});
            skLineSegment(sketch, "E317", {"start": v(-26.82, -4.32) * mm, "end": v(-26.97, -4.25) * mm});
            skLineSegment(sketch, "E318", {"start": v(-26.97, -4.25) * mm, "end": v(-27.1, -4.15) * mm});
            skLineSegment(sketch, "E319", {"start": v(-27.1, -4.15) * mm, "end": v(-27.15, -4.08) * mm});
            skLineSegment(sketch, "E320", {"start": v(-27.15, -4.08) * mm, "end": v(-25.98, 2.86) * mm});
            skLineSegment(sketch, "E321", {"start": v(-25.98, 2.86) * mm, "end": v(-25.42, 5.03) * mm});
            skLineSegment(sketch, "E322", {"start": v(-25.42, 5.03) * mm, "end": v(-25.37, 5.74) * mm});
            skLineSegment(sketch, "E323", {"start": v(-25.37, 5.74) * mm, "end": v(-25.5, 6.22) * mm});
            skLineSegment(sketch, "E324", {"start": v(-25.5, 6.22) * mm, "end": v(-25.78, 6.7) * mm});
            skLineSegment(sketch, "E325", {"start": v(-25.78, 6.7) * mm, "end": v(-26.5, 7.62) * mm});
            skLineSegment(sketch, "E326", {"start": v(-26.5, 7.62) * mm, "end": v(-26.64, 7.78) * mm});
            skLineSegment(sketch, "E327", {"start": v(-26.64, 7.78) * mm, "end": v(-26.8, 7.91) * mm});
            skLineSegment(sketch, "E328", {"start": v(-26.8, 7.91) * mm, "end": v(-27.18, 8.17) * mm});
            skLineSegment(sketch, "E329", {"start": v(-27.18, 8.17) * mm, "end": v(-26.71, 8.48) * mm});
            skLineSegment(sketch, "E330", {"start": v(-26.71, 8.48) * mm, "end": v(-26.55, 8.55) * mm});
            skLineSegment(sketch, "E331", {"start": v(-26.55, 8.55) * mm, "end": v(-1.97, 16.64) * mm});
            skLineSegment(sketch, "E332", {"start": v(-1.97, 16.64) * mm, "end": v(-2, 16.83) * mm});
            skLineSegment(sketch, "E333", {"start": v(30.2, 23.76) * mm, "end": v(30.2, 23.75) * mm});
            skLineSegment(sketch, "E334", {"start": v(30.2, 23.75) * mm, "end": v(30.28, 23.74) * mm});
            skLineSegment(sketch, "E335", {"start": v(30.28, 23.74) * mm, "end": v(30.43, 23.74) * mm});
            skLineSegment(sketch, "E336", {"start": v(30.43, 23.74) * mm, "end": v(30.61, 23.76) * mm});
            skLineSegment(sketch, "E337", {"start": v(30.61, 23.76) * mm, "end": v(30.76, 23.8) * mm});
            skLineSegment(sketch, "E338", {"start": v(30.76, 23.8) * mm, "end": v(30.9, 23.89) * mm});
            skLineSegment(sketch, "E339", {"start": v(30.9, 23.89) * mm, "end": v(31.18, 24.07) * mm});
            skLineSegment(sketch, "E340", {"start": v(31.18, 24.07) * mm, "end": v(30.95, 24.4) * mm});
            skLineSegment(sketch, "E341", {"start": v(30.95, 24.4) * mm, "end": v(30.84, 24.55) * mm});
            skLineSegment(sketch, "E342", {"start": v(30.84, 24.55) * mm, "end": v(30.7, 24.63) * mm});
            skLineSegment(sketch, "E343", {"start": v(30.7, 24.63) * mm, "end": v(-18.35, 34.72) * mm});
            skLineSegment(sketch, "E344", {"start": v(-18.35, 34.72) * mm, "end": v(-18.69, 34.76) * mm});
            skLineSegment(sketch, "E345", {"start": v(-18.69, 34.76) * mm, "end": v(-19.04, 34.75) * mm});
            skLineSegment(sketch, "E346", {"start": v(-19.04, 34.75) * mm, "end": v(-19.37, 34.7) * mm});
            skLineSegment(sketch, "E347", {"start": v(-19.37, 34.7) * mm, "end": v(-19.62, 34.56) * mm});
            skLineSegment(sketch, "E348", {"start": v(-19.62, 34.56) * mm, "end": v(-21, 33.23) * mm});
            skLineSegment(sketch, "E349", {"start": v(-21, 33.23) * mm, "end": v(-22.3, 31.83) * mm});
            skLineSegment(sketch, "E350", {"start": v(-22.3, 31.83) * mm, "end": v(-22.46, 31.6) * mm});
            skLineSegment(sketch, "E351", {"start": v(-22.46, 31.6) * mm, "end": v(-22.57, 31.32) * mm});
            skLineSegment(sketch, "E352", {"start": v(-22.57, 31.32) * mm, "end": v(-22.75, 30.73) * mm});
            skLineSegment(sketch, "E353", {"start": v(-22.75, 30.73) * mm, "end": v(30.2, 23.76) * mm});
            skLineSegment(sketch, "E354", {"start": v(-19.74, -29.96) * mm, "end": v(-17.5, -33.28) * mm});
            skLineSegment(sketch, "E355", {"start": v(-17.5, -33.28) * mm, "end": v(-17.41, -33.31) * mm});
            skLineSegment(sketch, "E356", {"start": v(-17.41, -33.31) * mm, "end": v(-17.27, -33.31) * mm});
            skLineSegment(sketch, "E357", {"start": v(-17.27, -33.31) * mm, "end": v(-17.13, -33.29) * mm});
            skLineSegment(sketch, "E358", {"start": v(-17.13, -33.29) * mm, "end": v(-17.05, -33.24) * mm});
            skLineSegment(sketch, "E359", {"start": v(-17.05, -33.24) * mm, "end": v(-6.02, -10.3) * mm});
            skLineSegment(sketch, "E360", {"start": v(-6.02, -10.3) * mm, "end": v(-6.02, -10.18) * mm});
            skLineSegment(sketch, "E361", {"start": v(-6.02, -10.18) * mm, "end": v(-6.08, -10.04) * mm});
            skLineSegment(sketch, "E362", {"start": v(-6.08, -10.04) * mm, "end": v(-6.27, -9.76) * mm});
            skLineSegment(sketch, "E363", {"start": v(-6.27, -9.76) * mm, "end": v(-6.32, -9.77) * mm});
            skLineSegment(sketch, "E364", {"start": v(-6.32, -9.77) * mm, "end": v(-6.43, -9.8) * mm});
            skLineSegment(sketch, "E365", {"start": v(-6.43, -9.8) * mm, "end": v(-6.55, -9.86) * mm});
            skLineSegment(sketch, "E366", {"start": v(-6.55, -9.86) * mm, "end": v(-6.63, -9.93) * mm});
            skLineSegment(sketch, "E367", {"start": v(-6.63, -9.93) * mm, "end": v(-19.74, -29.96) * mm});
            skLineSegment(sketch, "E368", {"start": v(-24.38, -12.74) * mm, "end": v(-24, -16.04) * mm});
            skLineSegment(sketch, "E369", {"start": v(-24, -16.04) * mm, "end": v(-24, -16.1) * mm});
            skLineSegment(sketch, "E370", {"start": v(-24, -16.1) * mm, "end": v(-23.96, -16.16) * mm});
            skLineSegment(sketch, "E371", {"start": v(-23.96, -16.16) * mm, "end": v(-23.9, -16.27) * mm});
            skLineSegment(sketch, "E372", {"start": v(-23.9, -16.27) * mm, "end": v(-23.75, -16.2) * mm});
            skLineSegment(sketch, "E373", {"start": v(-23.75, -16.2) * mm, "end": v(-23.69, -16.18) * mm});
            skLineSegment(sketch, "E374", {"start": v(-23.69, -16.18) * mm, "end": v(-23.63, -16.13) * mm});
            skLineSegment(sketch, "E375", {"start": v(-23.63, -16.13) * mm, "end": v(-9.02, 0.22) * mm});
            skLineSegment(sketch, "E376", {"start": v(-9.02, 0.22) * mm, "end": v(-8.98, 0.31) * mm});
            skLineSegment(sketch, "E377", {"start": v(-8.98, 0.31) * mm, "end": v(-8.96, 0.42) * mm});
            skLineSegment(sketch, "E378", {"start": v(-8.96, 0.42) * mm, "end": v(-8.93, 0.65) * mm});
            skLineSegment(sketch, "E379", {"start": v(-8.93, 0.65) * mm, "end": v(-9.04, 0.65) * mm});
            skLineSegment(sketch, "E380", {"start": v(-9.04, 0.65) * mm, "end": v(-9.09, 0.64) * mm});
            skLineSegment(sketch, "E381", {"start": v(-9.09, 0.64) * mm, "end": v(-9.13, 0.63) * mm});
            skLineSegment(sketch, "E382", {"start": v(-9.13, 0.63) * mm, "end": v(-21.96, -10) * mm});
            skLineSegment(sketch, "E383", {"start": v(-21.96, -10) * mm, "end": v(-23.62, -11.12) * mm});
            skLineSegment(sketch, "E384", {"start": v(-23.62, -11.12) * mm, "end": v(-24.24, -11.8) * mm});
            skLineSegment(sketch, "E385", {"start": v(-24.24, -11.8) * mm, "end": v(-24.38, -12.74) * mm});
            skLineSegment(sketch, "E386", {"start": v(-6.92, 11.48) * mm, "end": v(-22.15, 6.07) * mm});
            skLineSegment(sketch, "E387", {"start": v(-22.15, 6.07) * mm, "end": v(-22.42, 5.95) * mm});
            skLineSegment(sketch, "E388", {"start": v(-22.42, 5.95) * mm, "end": v(-22.68, 5.8) * mm});
            skLineSegment(sketch, "E389", {"start": v(-22.68, 5.8) * mm, "end": v(-22.9, 5.62) * mm});
            skLineSegment(sketch, "E390", {"start": v(-22.9, 5.62) * mm, "end": v(-23.02, 5.41) * mm});
            skLineSegment(sketch, "E391", {"start": v(-23.02, 5.41) * mm, "end": v(-23.63, 2.15) * mm});
            skLineSegment(sketch, "E392", {"start": v(-23.63, 2.15) * mm, "end": v(-23.63, 2.07) * mm});
            skLineSegment(sketch, "E393", {"start": v(-23.63, 2.07) * mm, "end": v(-23.63, 2) * mm});
            skLineSegment(sketch, "E394", {"start": v(-23.63, 2) * mm, "end": v(-23.6, 1.91) * mm});
            skLineSegment(sketch, "E395", {"start": v(-23.6, 1.91) * mm, "end": v(-23.58, 1.84) * mm});
            skLineSegment(sketch, "E396", {"start": v(-23.58, 1.84) * mm, "end": v(-23.56, 1.83) * mm});
            skLineSegment(sketch, "E397", {"start": v(-23.56, 1.83) * mm, "end": v(-23.5, 1.83) * mm});
            skLineSegment(sketch, "E398", {"start": v(-23.5, 1.83) * mm, "end": v(-23.44, 1.83) * mm});
            skLineSegment(sketch, "E399", {"start": v(-23.44, 1.83) * mm, "end": v(-23.38, 1.85) * mm});
            skLineSegment(sketch, "E400", {"start": v(-23.38, 1.85) * mm, "end": v(-7.1, 10.58) * mm});
            skLineSegment(sketch, "E401", {"start": v(-7.1, 10.58) * mm, "end": v(-6.96, 10.7) * mm});
            skLineSegment(sketch, "E402", {"start": v(-6.96, 10.7) * mm, "end": v(-6.86, 10.9) * mm});
            skLineSegment(sketch, "E403", {"start": v(-6.86, 10.9) * mm, "end": v(-6.7, 11.31) * mm});
            skLineSegment(sketch, "E404", {"start": v(-6.7, 11.31) * mm, "end": v(-6.71, 11.34) * mm});
            skLineSegment(sketch, "E405", {"start": v(-6.71, 11.34) * mm, "end": v(-6.92, 11.48) * mm});
            skLineSegment(sketch, "E406", {"start": v(-14.95, 20.02) * mm, "end": v(-15.97, 19.9) * mm});
            skLineSegment(sketch, "E407", {"start": v(-15.97, 19.9) * mm, "end": v(-16.59, 19.34) * mm});
            skLineSegment(sketch, "E408", {"start": v(-16.59, 19.34) * mm, "end": v(-17.4, 17.83) * mm});
            skLineSegment(sketch, "E409", {"start": v(-17.4, 17.83) * mm, "end": v(-17.54, 17.6) * mm});
            skLineSegment(sketch, "E410", {"start": v(-17.54, 17.6) * mm, "end": v(-17.92, 16.88) * mm});
            skLineSegment(sketch, "E411", {"start": v(-17.92, 16.88) * mm, "end": v(-16.93, 16.87) * mm});
            skLineSegment(sketch, "E412", {"start": v(-16.93, 16.87) * mm, "end": v(-16.6, 16.89) * mm});
            skLineSegment(sketch, "E413", {"start": v(-16.6, 16.89) * mm, "end": v(-16.3, 16.94) * mm});
            skLineSegment(sketch, "E414", {"start": v(-16.3, 16.94) * mm, "end": v(-15.7, 17.08) * mm});
            skLineSegment(sketch, "E415", {"start": v(-15.7, 17.08) * mm, "end": v(-3.05, 19.37) * mm});
            skLineSegment(sketch, "E416", {"start": v(-3.05, 19.37) * mm, "end": v(-2.69, 19.48) * mm});
            skLineSegment(sketch, "E417", {"start": v(-2.69, 19.48) * mm, "end": v(-1.65, 20) * mm});
            skLineSegment(sketch, "E418", {"start": v(-1.65, 20) * mm, "end": v(-14.95, 20.02) * mm});
            skLineSegment(sketch, "E419", {"start": v(46.54, 16.29) * mm, "end": v(46.64, 17.52) * mm});
            skLineSegment(sketch, "E420", {"start": v(46.64, 17.52) * mm, "end": v(46.3, 18.9) * mm});
            skLineSegment(sketch, "E421", {"start": v(46.3, 18.9) * mm, "end": v(45.6, 20.23) * mm});
            skLineSegment(sketch, "E422", {"start": v(45.6, 20.23) * mm, "end": v(44.62, 21.24) * mm});
            skLineSegment(sketch, "E423", {"start": v(44.62, 21.24) * mm, "end": v(43.69, 21.83) * mm});
            skLineSegment(sketch, "E424", {"start": v(43.69, 21.83) * mm, "end": v(43.64, 21.24) * mm});
            skLineSegment(sketch, "E425", {"start": v(43.64, 21.24) * mm, "end": v(43.6, 20.95) * mm});
            skLineSegment(sketch, "E426", {"start": v(43.6, 20.95) * mm, "end": v(43.53, 20.67) * mm});
            skLineSegment(sketch, "E427", {"start": v(43.53, 20.67) * mm, "end": v(43.42, 20.47) * mm});
            skLineSegment(sketch, "E428", {"start": v(43.42, 20.47) * mm, "end": v(43.27, 20.28) * mm});
            skLineSegment(sketch, "E429", {"start": v(43.27, 20.28) * mm, "end": v(43.08, 20.12) * mm});
            skLineSegment(sketch, "E430", {"start": v(43.08, 20.12) * mm, "end": v(42.9, 20.04) * mm});
            skLineSegment(sketch, "E431", {"start": v(42.9, 20.04) * mm, "end": v(36.2, 19.29) * mm});
            skLineSegment(sketch, "E432", {"start": v(36.2, 19.29) * mm, "end": v(35.81, 19.22) * mm});
            skLineSegment(sketch, "E433", {"start": v(35.81, 19.22) * mm, "end": v(34.63, 18.88) * mm});
            skLineSegment(sketch, "E434", {"start": v(34.63, 18.88) * mm, "end": v(43.03, 18.36) * mm});
            skLineSegment(sketch, "E435", {"start": v(43.03, 18.36) * mm, "end": v(44.37, 18.09) * mm});
            skLineSegment(sketch, "E436", {"start": v(44.37, 18.09) * mm, "end": v(45.57, 17.45) * mm});
            skLineSegment(sketch, "E437", {"start": v(45.57, 17.45) * mm, "end": v(46.54, 16.29) * mm});
            skLineSegment(sketch, "E438", {"start": v(40.29, 21.23) * mm, "end": v(41.55, 21.24) * mm});
            skLineSegment(sketch, "E439", {"start": v(41.55, 21.24) * mm, "end": v(41.64, 21.25) * mm});
            skLineSegment(sketch, "E440", {"start": v(41.64, 21.25) * mm, "end": v(41.92, 21.35) * mm});
            skLineSegment(sketch, "E441", {"start": v(41.92, 21.35) * mm, "end": v(41.75, 21.53) * mm});
            skLineSegment(sketch, "E442", {"start": v(41.75, 21.53) * mm, "end": v(39.5, 23.44) * mm});
            skLineSegment(sketch, "E443", {"start": v(39.5, 23.44) * mm, "end": v(38.74, 24) * mm});
            skLineSegment(sketch, "E444", {"start": v(38.74, 24) * mm, "end": v(37.95, 24.46) * mm});
            skLineSegment(sketch, "E445", {"start": v(37.95, 24.46) * mm, "end": v(35.46, 25.65) * mm});
            skLineSegment(sketch, "E446", {"start": v(35.46, 25.65) * mm, "end": v(35.37, 25.66) * mm});
            skLineSegment(sketch, "E447", {"start": v(35.37, 25.66) * mm, "end": v(35.26, 25.64) * mm});
            skLineSegment(sketch, "E448", {"start": v(35.26, 25.64) * mm, "end": v(35.03, 25.57) * mm});
            skLineSegment(sketch, "E449", {"start": v(35.03, 25.57) * mm, "end": v(37.92, 22.7) * mm});
            skLineSegment(sketch, "E450", {"start": v(37.92, 22.7) * mm, "end": v(38.86, 21.47) * mm});
            skLineSegment(sketch, "E451", {"start": v(38.86, 21.47) * mm, "end": v(39.44, 21.1) * mm});
            skLineSegment(sketch, "E452", {"start": v(39.44, 21.1) * mm, "end": v(40.29, 21.23) * mm});
            skLineSegment(sketch, "E453", {"start": v(11.36, 0.44) * mm, "end": v(6.85, 0.45) * mm});
            skLineSegment(sketch, "E454", {"start": v(6.85, 0.45) * mm, "end": v(6.71, 0.46) * mm});
            skLineSegment(sketch, "E455", {"start": v(6.71, 0.46) * mm, "end": v(6.56, 0.5) * mm});
            skLineSegment(sketch, "E456", {"start": v(6.56, 0.5) * mm, "end": v(6.44, 0.57) * mm});
            skLineSegment(sketch, "E457", {"start": v(6.44, 0.57) * mm, "end": v(6.35, 0.66) * mm});
            skLineSegment(sketch, "E458", {"start": v(6.35, 0.66) * mm, "end": v(6.34, 0.75) * mm});
            skLineSegment(sketch, "E459", {"start": v(6.34, 0.75) * mm, "end": v(6.37, 0.89) * mm});
            skLineSegment(sketch, "E460", {"start": v(6.37, 0.89) * mm, "end": v(10.6, 9.32) * mm});
            skLineSegment(sketch, "E461", {"start": v(10.6, 9.32) * mm, "end": v(12.6, 14.31) * mm});
            skLineSegment(sketch, "E462", {"start": v(12.6, 14.31) * mm, "end": v(12.7, 14.36) * mm});
            skLineSegment(sketch, "E463", {"start": v(12.7, 14.36) * mm, "end": v(12.93, 14.37) * mm});
            skLineSegment(sketch, "E464", {"start": v(12.93, 14.37) * mm, "end": v(13.18, 14.34) * mm});
            skLineSegment(sketch, "E465", {"start": v(13.18, 14.34) * mm, "end": v(13.39, 14.27) * mm});
            skLineSegment(sketch, "E466", {"start": v(13.39, 14.27) * mm, "end": v(22.27, 9.33) * mm});
            skLineSegment(sketch, "E467", {"start": v(22.27, 9.33) * mm, "end": v(31.2, 2.48) * mm});
            skLineSegment(sketch, "E468", {"start": v(31.2, 2.48) * mm, "end": v(31.88, 1.46) * mm});
            skLineSegment(sketch, "E469", {"start": v(31.88, 1.46) * mm, "end": v(31.55, 0.74) * mm});
            skLineSegment(sketch, "E470", {"start": v(31.55, 0.74) * mm, "end": v(30.77, 0.24) * mm});
            skLineSegment(sketch, "E471", {"start": v(30.77, 0.24) * mm, "end": v(30.08, -0.12) * mm});
            skLineSegment(sketch, "E472", {"start": v(30.08, -0.12) * mm, "end": v(28.87, -0.86) * mm});
            skLineSegment(sketch, "E473", {"start": v(28.87, -0.86) * mm, "end": v(24.95, -2.66) * mm});
            skLineSegment(sketch, "E474", {"start": v(24.95, -2.66) * mm, "end": v(24.87, -2.67) * mm});
            skLineSegment(sketch, "E475", {"start": v(24.87, -2.67) * mm, "end": v(24.78, -2.64) * mm});
            skLineSegment(sketch, "E476", {"start": v(24.78, -2.64) * mm, "end": v(24.58, -2.57) * mm});
            skLineSegment(sketch, "E477", {"start": v(24.58, -2.57) * mm, "end": v(24.63, -2.34) * mm});
            skLineSegment(sketch, "E478", {"start": v(24.63, -2.34) * mm, "end": v(24.66, -2.24) * mm});
            skLineSegment(sketch, "E479", {"start": v(24.66, -2.24) * mm, "end": v(24.7, -2.14) * mm});
            skLineSegment(sketch, "E480", {"start": v(24.7, -2.14) * mm, "end": v(25.7, -0.86) * mm});
            skLineSegment(sketch, "E481", {"start": v(25.7, -0.86) * mm, "end": v(26, -0.41) * mm});
            skLineSegment(sketch, "E482", {"start": v(26, -0.41) * mm, "end": v(25.98, -0.23) * mm});
            skLineSegment(sketch, "E483", {"start": v(25.98, -0.23) * mm, "end": v(25.86, 0.04) * mm});
            skLineSegment(sketch, "E484", {"start": v(25.86, 0.04) * mm, "end": v(25.68, 0.28) * mm});
            skLineSegment(sketch, "E485", {"start": v(25.68, 0.28) * mm, "end": v(25.53, 0.38) * mm});
            skLineSegment(sketch, "E486", {"start": v(25.53, 0.38) * mm, "end": v(21.76, 0.19) * mm});
            skLineSegment(sketch, "E487", {"start": v(21.76, 0.19) * mm, "end": v(20.53, 0.02) * mm});
            skLineSegment(sketch, "E488", {"start": v(20.53, 0.02) * mm, "end": v(20.32, -0.2) * mm});
            skLineSegment(sketch, "E489", {"start": v(20.32, -0.2) * mm, "end": v(20.16, -0.69) * mm});
            skLineSegment(sketch, "E490", {"start": v(20.16, -0.69) * mm, "end": v(19.95, -1.85) * mm});
            skLineSegment(sketch, "E491", {"start": v(19.95, -1.85) * mm, "end": v(19.93, -2.22) * mm});
            skLineSegment(sketch, "E492", {"start": v(19.93, -2.22) * mm, "end": v(20.1, -3.35) * mm});
            skLineSegment(sketch, "E493", {"start": v(20.1, -3.35) * mm, "end": v(19.14, -3) * mm});
            skLineSegment(sketch, "E494", {"start": v(19.14, -3) * mm, "end": v(18.7, -2.8) * mm});
            skLineSegment(sketch, "E495", {"start": v(18.7, -2.8) * mm, "end": v(18.33, -2.52) * mm});
            skLineSegment(sketch, "E496", {"start": v(18.33, -2.52) * mm, "end": v(17.8, -1.86) * mm});
            skLineSegment(sketch, "E497", {"start": v(17.8, -1.86) * mm, "end": v(16.36, 0.28) * mm});
            skLineSegment(sketch, "E498", {"start": v(16.36, 0.28) * mm, "end": v(16.29, 0.34) * mm});
            skLineSegment(sketch, "E499", {"start": v(16.29, 0.34) * mm, "end": v(16.19, 0.39) * mm});
            skLineSegment(sketch, "E500", {"start": v(16.19, 0.39) * mm, "end": v(16.07, 0.41) * mm});
            skLineSegment(sketch, "E501", {"start": v(16.07, 0.41) * mm, "end": v(15.96, 0.42) * mm});
            skLineSegment(sketch, "E502", {"start": v(15.96, 0.42) * mm, "end": v(11.36, 0.43) * mm});
            skLineSegment(sketch, "E503", {"start": v(11.36, 0.43) * mm, "end": v(11.36, 0.44) * mm});
            skLineSegment(sketch, "E504", {"start": v(16.18, 2) * mm, "end": v(22.25, 2.02) * mm});
            skLineSegment(sketch, "E505", {"start": v(22.25, 2.02) * mm, "end": v(22.37, 2.06) * mm});
            skLineSegment(sketch, "E506", {"start": v(22.37, 2.06) * mm, "end": v(22.48, 2.14) * mm});
            skLineSegment(sketch, "E507", {"start": v(22.48, 2.14) * mm, "end": v(22.7, 2.36) * mm});
            skLineSegment(sketch, "E508", {"start": v(22.7, 2.36) * mm, "end": v(22.69, 2.4) * mm});
            skLineSegment(sketch, "E509", {"start": v(22.69, 2.4) * mm, "end": v(22.65, 2.49) * mm});
            skLineSegment(sketch, "E510", {"start": v(22.65, 2.49) * mm, "end": v(22.6, 2.57) * mm});
            skLineSegment(sketch, "E511", {"start": v(22.6, 2.57) * mm, "end": v(22.54, 2.6) * mm});
            skLineSegment(sketch, "E512", {"start": v(22.54, 2.6) * mm, "end": v(11.51, 4.46) * mm});
            skLineSegment(sketch, "E513", {"start": v(11.51, 4.46) * mm, "end": v(11.3, 4.46) * mm});
            skLineSegment(sketch, "E514", {"start": v(11.3, 4.46) * mm, "end": v(11.1, 4.39) * mm});
            skLineSegment(sketch, "E515", {"start": v(11.1, 4.39) * mm, "end": v(10.9, 4.28) * mm});
            skLineSegment(sketch, "E516", {"start": v(10.9, 4.28) * mm, "end": v(10.74, 4.14) * mm});
            skLineSegment(sketch, "E517", {"start": v(10.74, 4.14) * mm, "end": v(10.56, 3.86) * mm});
            skLineSegment(sketch, "E518", {"start": v(10.56, 3.86) * mm, "end": v(9.92, 2.5) * mm});
            skLineSegment(sketch, "E519", {"start": v(9.92, 2.5) * mm, "end": v(9.89, 2.2) * mm});
            skLineSegment(sketch, "E520", {"start": v(9.89, 2.2) * mm, "end": v(10.11, 2.02) * mm});
            skLineSegment(sketch, "E521", {"start": v(10.11, 2.02) * mm, "end": v(10.68, 1.98) * mm});
            skLineSegment(sketch, "E522", {"start": v(10.68, 1.98) * mm, "end": v(16.18, 2) * mm});
            skSolve(sketch);
        }
        {
            var Q0;
            Q0=makeQuery(id+"F0.imprint","IMPRINT",FACE,{"disambiguationData":[TD([[makeQuery(id+"F0.imprint","IMPRINT",EDGE,{"derivedFrom":sQuery(id+"F0.wireOp",EDGE,"E0")}),-1.0]])]});
            var Q1;
            Q1=makeQuery(id+"F0.imprint","IMPRINT",FACE,{"disambiguationData":[TD([[makeQuery(id+"F0.imprint","IMPRINT",EDGE,{"derivedFrom":sQuery(id+"F0.wireOp",EDGE,"E100")}),1.0]])]});
            var Q2;
            Q2=makeQuery(id+"F0.imprint","IMPRINT",FACE,{"disambiguationData":[TD([[makeQuery(id+"F0.imprint","IMPRINT",EDGE,{"derivedFrom":sQuery(id+"F0.wireOp",EDGE,"E201")}),-1.0]])]});
            var Q3;
            Q3=makeQuery(id+"F0.imprint","IMPRINT",FACE,{"disambiguationData":[TD([[makeQuery(id+"F0.imprint","IMPRINT",EDGE,{"derivedFrom":sQuery(id+"F0.wireOp",EDGE,"E333")}),1.0]])]});
            var Q4;
            Q4=makeQuery(id+"F0.imprint","IMPRINT",FACE,{"disambiguationData":[TD([[makeQuery(id+"F0.imprint","IMPRINT",EDGE,{"derivedFrom":sQuery(id+"F0.wireOp",EDGE,"E406")}),1.0]])]});
            var Q5;
            Q5=makeQuery(id+"F0.imprint","IMPRINT",FACE,{"disambiguationData":[TD([[makeQuery(id+"F0.imprint","IMPRINT",EDGE,{"derivedFrom":sQuery(id+"F0.wireOp",EDGE,"E386")}),1.0]])]});
            var Q6;
            Q6=makeQuery(id+"F0.imprint","IMPRINT",FACE,{"disambiguationData":[TD([[makeQuery(id+"F0.imprint","IMPRINT",EDGE,{"derivedFrom":sQuery(id+"F0.wireOp",EDGE,"E368")}),1.0]])]});
            var Q7;
            Q7=makeQuery(id+"F0.imprint","IMPRINT",FACE,{"disambiguationData":[TD([[makeQuery(id+"F0.imprint","IMPRINT",EDGE,{"derivedFrom":sQuery(id+"F0.wireOp",EDGE,"E354")}),1.0]])]});
            var Q8;
            Q8=makeQuery(id+"F0.imprint","IMPRINT",FACE,{"disambiguationData":[TD([[makeQuery(id+"F0.imprint","IMPRINT",EDGE,{"derivedFrom":sQuery(id+"F0.wireOp",EDGE,"E453")}),-1.0]])]});
            var Q9;
            Q9=makeQuery(id+"F0.imprint","IMPRINT",FACE,{"disambiguationData":[TD([[makeQuery(id+"F0.imprint","IMPRINT",EDGE,{"derivedFrom":sQuery(id+"F0.wireOp",EDGE,"E504")}),1.0]])]});
            var Q10;
            Q10=makeQuery(id+"F0.imprint","IMPRINT",FACE,{"disambiguationData":[TD([[makeQuery(id+"F0.imprint","IMPRINT",EDGE,{"derivedFrom":sQuery(id+"F0.wireOp",EDGE,"E438")}),1.0]])]});
            var Q11;
            Q11=makeQuery(id+"F0.imprint","IMPRINT",FACE,{"disambiguationData":[TD([[makeQuery(id+"F0.imprint","IMPRINT",EDGE,{"derivedFrom":sQuery(id+"F0.wireOp",EDGE,"E419")}),1.0]])]});
            extrude(context, id + "F1", {"entities" : qUnion([Q0, Q1, Q2, Q3, Q4, Q5, Q6, Q7, Q8, Q9, Q10, Q11]), "endBound" : BoundingType.SYMMETRIC, "depth" : 1 * mm});
        }
        {
            var Q0;
            Q0=makeQuery(id+"F0.imprint","IMPRINT",FACE,{"disambiguationData":[TD([[makeQuery(id+"F0.imprint","IMPRINT",EDGE,{"derivedFrom":sQuery(id+"F0.wireOp",EDGE,"E0")}),-1.0]])]});
            var Q1;
            Q1=makeQuery(id+"F0.imprint","IMPRINT",FACE,{"disambiguationData":[TD([[makeQuery(id+"F0.imprint","IMPRINT",EDGE,{"derivedFrom":sQuery(id+"F0.wireOp",EDGE,"E201")}),-1.0]])]});
            var Q2;
            Q2=makeQuery(id+"F0.imprint","IMPRINT",FACE,{"disambiguationData":[TD([[makeQuery(id+"F0.imprint","IMPRINT",EDGE,{"derivedFrom":sQuery(id+"F0.wireOp",EDGE,"E453")}),-1.0]])]});
            extrude(context, id + "F2", {"entities" : qUnion([Q0, Q1, Q2]), "endBound" : BoundingType.SYMMETRIC, "depth" : 1 * mm});
        }
    });
